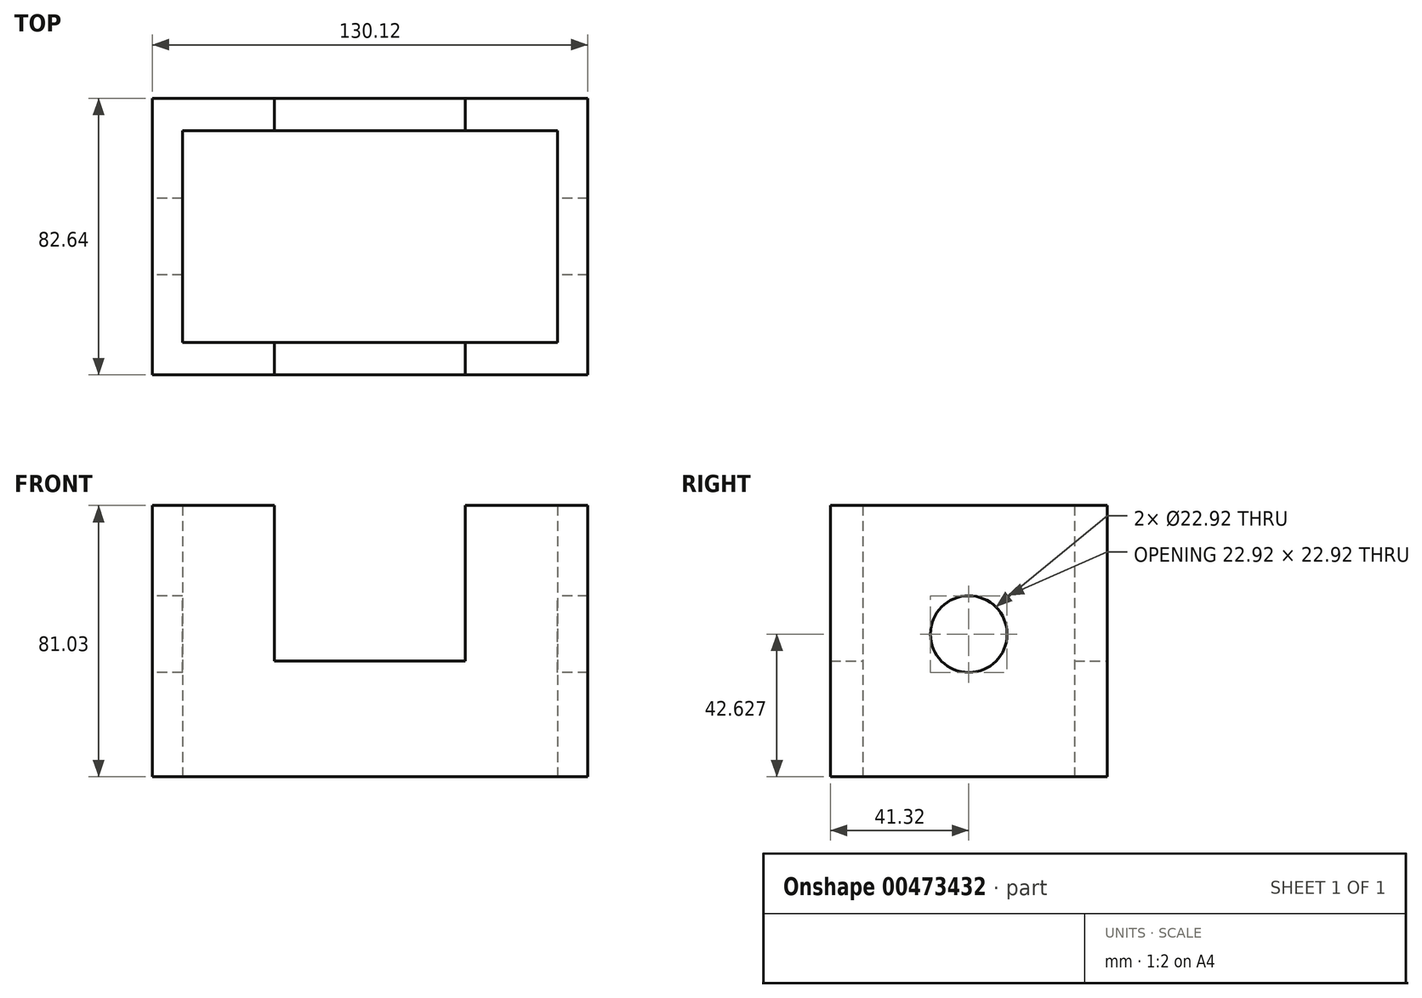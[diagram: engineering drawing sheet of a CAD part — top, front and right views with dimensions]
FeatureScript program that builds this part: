
annotation { "Feature Type Name" : "Feature", "Feature Type Description" : "" }
export const myFeature = defineFeature(function(context is Context, id is Id, definition is map)
    precondition{}
    {
        {
            var Q0;
            Q0=qCreatedBy(makeId("Top.planeOp"),FACE);
            var sketch = newSketch(context, id + "F0", { "sketchPlane" : qUnion([Q0])});
            skLineSegment(sketch, "E0.bottom", {"start": v(65.06, -41.32) * mm, "end": v(-65.06, -41.32) * mm});
            skLineSegment(sketch, "E0.top", {"start": v(65.06, 41.32) * mm, "end": v(-65.06, 41.32) * mm});
            skLineSegment(sketch, "E0.left", {"start": v(65.06, -41.32) * mm, "end": v(65.06, 41.32) * mm});
            skLineSegment(sketch, "E0.right", {"start": v(-65.06, -41.32) * mm, "end": v(-65.06, 41.32) * mm});
            skPoint(sketch, "E0.middle", {"position": v(0, 0) * mm});
            skSolve(sketch);
        }
        {
            var Q0;
            Q0=makeQuery(id+"F0.imprint","IMPRINT",FACE,{"disambiguationData":[TD([[makeQuery(id+"F0.imprint","IMPRINT",EDGE,{"derivedFrom":sQuery(id+"F0.wireOp",EDGE,"E0.bottom")}),-1.0]])]});
            var sketch = newSketch(context, id + "F1", { "sketchPlane" : qUnion([Q0])});
            skLineSegment(sketch, "E1.bottom", {"start": v(-56, 31.62) * mm, "end": v(56, 31.62) * mm});
            skLineSegment(sketch, "E1.top", {"start": v(-56, -31.62) * mm, "end": v(56, -31.62) * mm});
            skLineSegment(sketch, "E1.left", {"start": v(-56, 31.62) * mm, "end": v(-56, -31.62) * mm});
            skLineSegment(sketch, "E1.right", {"start": v(56, 31.62) * mm, "end": v(56, -31.62) * mm});
            skPoint(sketch, "E1.middle", {"position": v(0, 0) * mm});
            skSolve(sketch);
        }
        {
            var Q0;
            Q0=makeQuery(id+"F1.imprint","IMPRINT",FACE,{"disambiguationData":[TD([[makeQuery(id+"F1.imprint","IMPRINT",EDGE,{"derivedFrom":sQuery(id+"F1.wireOp",EDGE,"E1.bottom")}),1.0]])]});
            extrude(context, id + "F2", {"entities" : qUnion([Q0]), "depth" : 81.03 * mm});
        }
        {
            var Q0;
            Q0=makeQuery(id+"F2.opExtrude","SWEPT_FACE",FACE,{"disambiguationData":[OSD([sQuery(id+"F0.wireOp",EDGE,"E0.top")])]});
            var sketch = newSketch(context, id + "F3", { "sketchPlane" : qUnion([Q0])});
            skLineSegment(sketch, "E2.bottom", {"start": v(-28.42, 81.03) * mm, "end": v(28.62, 81.03) * mm});
            skLineSegment(sketch, "E2.top", {"start": v(-28.42, 34.56) * mm, "end": v(28.62, 34.56) * mm});
            skLineSegment(sketch, "E2.left", {"start": v(-28.42, 81.03) * mm, "end": v(-28.42, 34.56) * mm});
            skLineSegment(sketch, "E2.right", {"start": v(28.62, 81.03) * mm, "end": v(28.62, 34.56) * mm});
            skSolve(sketch);
        }
        {
            var Q0;
            Q0=makeQuery(id+"F3.imprint","IMPRINT",FACE,{"disambiguationData":[TD([[makeQuery(id+"F3.imprint","IMPRINT",EDGE,{"derivedFrom":sQuery(id+"F3.wireOp",EDGE,"E2.bottom")}),-1.0]])]});
            extrude(context, id + "F4", {"entities" : qUnion([Q0]), "operationType" : NewBodyOperationType.REMOVE, "oppositeDirection" : true, "depth" : 105.16 * mm});
        }
        {
            var Q0;
            Q0=makeQuery(id+"F2.opExtrude","SWEPT_FACE",FACE,{"disambiguationData":[OSD([sQuery(id+"F0.wireOp",EDGE,"E0.right")])]});
            var sketch = newSketch(context, id + "F5", { "sketchPlane" : qUnion([Q0])});
            skCircle(sketch, "E3", {"center": v(0, 42.63) * mm, "radius": 11.46 * mm});
            skSolve(sketch);
        }
        {
            var Q0;
            Q0=makeQuery(id+"F5.imprint","IMPRINT",FACE,{"disambiguationData":[TD([[makeQuery(id+"F5.imprint","IMPRINT",EDGE,{"derivedFrom":sQuery(id+"F5.wireOp",EDGE,"E3")}),1.0]])]});
            extrude(context, id + "F6", {"entities" : qUnion([Q0]), "operationType" : NewBodyOperationType.REMOVE, "oppositeDirection" : true, "depth" : 164.34 * mm});
        }
    });
